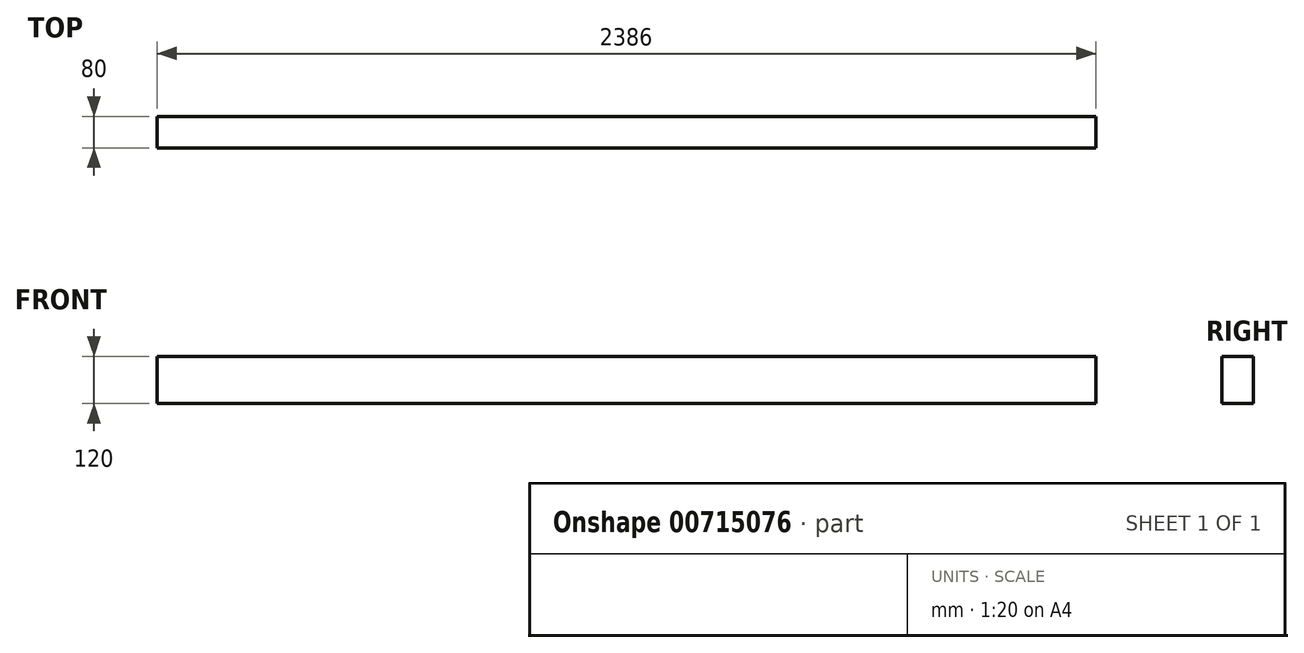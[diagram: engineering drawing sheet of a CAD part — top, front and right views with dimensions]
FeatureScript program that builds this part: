
annotation { "Feature Type Name" : "Feature", "Feature Type Description" : "" }
export const myFeature = defineFeature(function(context is Context, id is Id, definition is map)
    precondition{}
    {
        {
            var Q0;
            Q0=qCreatedBy(makeId("Right.planeOp"),FACE);
            var sketch = newSketch(context, id + "F0", { "sketchPlane" : qUnion([Q0])});
            skLineSegment(sketch, "E0.bottom", {"start": v(-40, 60) * mm, "end": v(40, 60) * mm});
            skLineSegment(sketch, "E0.top", {"start": v(-40, -60) * mm, "end": v(40, -60) * mm});
            skLineSegment(sketch, "E0.left", {"start": v(-40, 60) * mm, "end": v(-40, -60) * mm});
            skLineSegment(sketch, "E0.right", {"start": v(40, 60) * mm, "end": v(40, -60) * mm});
            skPoint(sketch, "E0.middle", {"position": v(0, 0) * mm});
            skSolve(sketch);
        }
        {
            var Q0;
            Q0=makeQuery(id+"F0.imprint","IMPRINT",FACE,{"disambiguationData":[TD([[makeQuery(id+"F0.imprint","IMPRINT",EDGE,{"derivedFrom":sQuery(id+"F0.wireOp",EDGE,"E0.bottom")}),-1.0]])]});
            extrude(context, id + "F1", {"entities" : qUnion([Q0]), "depth" : (2550 - 80 - 80 - 4) * mm, "offsetDistance" : 25 * mm});
        }
    });
